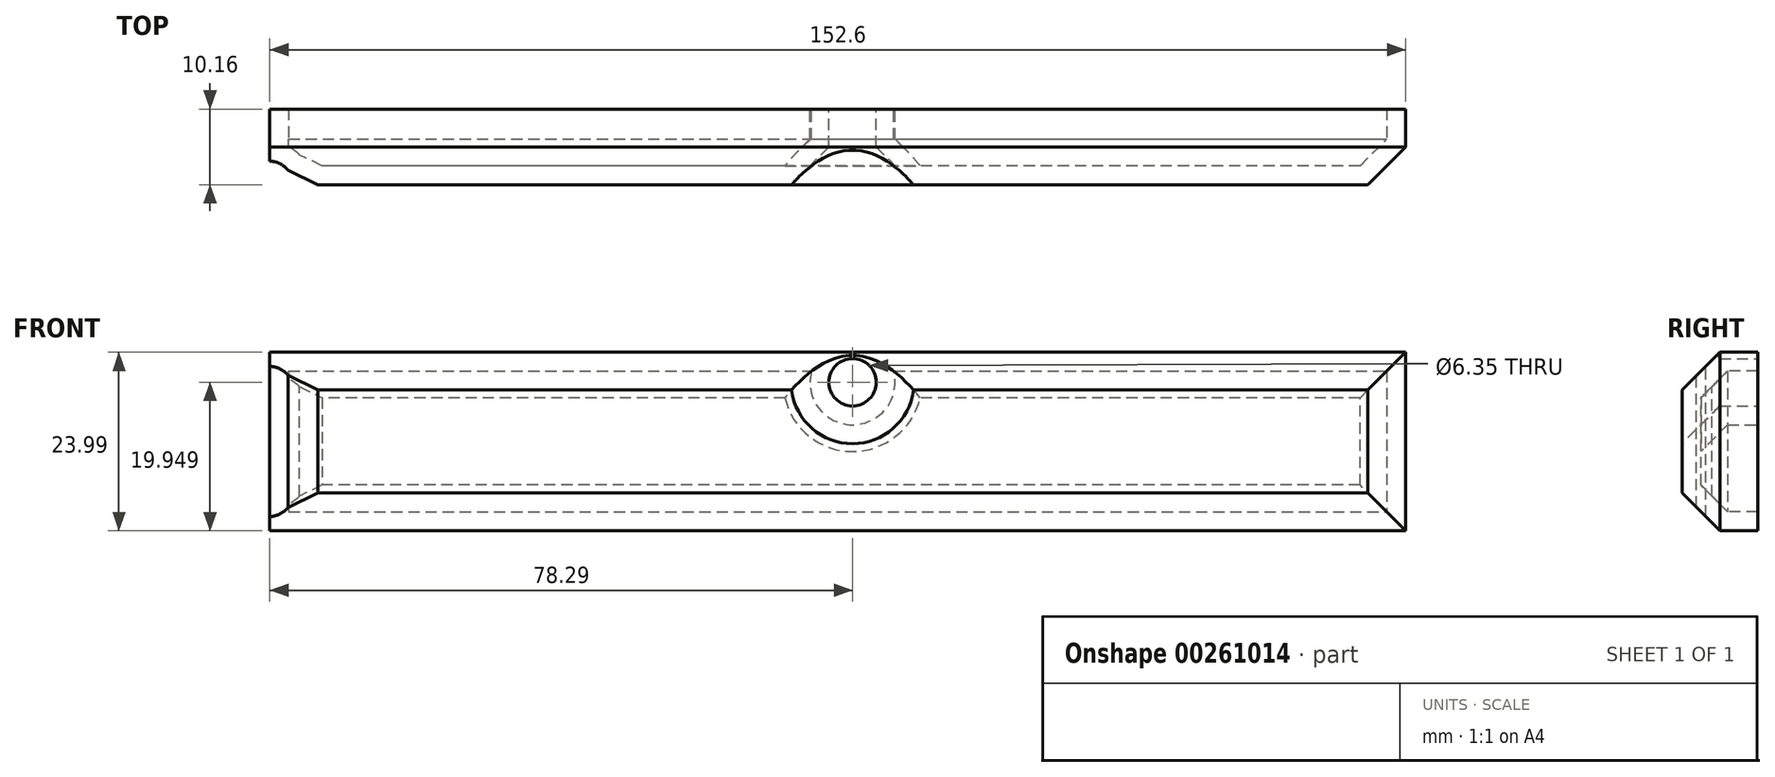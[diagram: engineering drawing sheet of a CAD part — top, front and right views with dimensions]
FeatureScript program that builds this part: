
annotation { "Feature Type Name" : "Feature", "Feature Type Description" : "" }
export const myFeature = defineFeature(function(context is Context, id is Id, definition is map)
    precondition{}
    {
        {
            var Q0;
            Q0=qCreatedBy(makeId("Front.planeOp"),FACE);
            var sketch = newSketch(context, id + "F0", { "sketchPlane" : qUnion([Q0])});
            skLineSegment(sketch, "E0", {"start": v(0, 0) * mm, "end": v(-76.65, 0) * mm});
            skLineSegment(sketch, "E1", {"start": v(0, 0) * mm, "end": v(75.95, 0) * mm});
            skLineSegment(sketch, "E2", {"start": v(-76.65, 0) * mm, "end": v(-76.65, -23.99) * mm});
            skLineSegment(sketch, "E3", {"start": v(75.95, 0) * mm, "end": v(75.95, -23.99) * mm});
            skLineSegment(sketch, "E4", {"start": v(-76.65, -23.99) * mm, "end": v(75.95, -23.99) * mm});
            skSolve(sketch);
        }
        {
            var Q0;
            Q0=qCreatedBy(makeId("Top.planeOp"),FACE);
            var sketch = newSketch(context, id + "F1", { "sketchPlane" : qUnion([Q0])});
            skLineSegment(sketch, "E5", {"start": v(-76.7, 0) * mm, "end": v(-76.7, 10.03) * mm});
            skLineSegment(sketch, "E6", {"start": v(75.65, 0) * mm, "end": v(75.65, 10.03) * mm});
            skLineSegment(sketch, "E7", {"start": v(-76.7, 10.03) * mm, "end": v(75.65, 10.03) * mm});
            skSolve(sketch);
        }
        {
            var Q0;
            Q0=makeQuery(id+"F0.imprint","IMPRINT",FACE,{"disambiguationData":[TD([[makeQuery(id+"F0.imprint","IMPRINT",EDGE,{"derivedFrom":sQuery(id+"F0.wireOp",EDGE,"E0")}),1.0]])]});
            extrude(context, id + "F2", {"entities" : qUnion([Q0]), "oppositeDirection" : true, "depth" : 10.16 * mm});
        }
        {
            var Q0;
            Q0=sQuery(id+"F1.wireOp",VERTEX,"E5.start");
            var Q1;
            Q1=makeQuery(id+"F2.opExtrude","SWEPT_BODY",BODY,{"disambiguationData":[OSD([sQuery(id+"F0.wireOp",EDGE,"E0"),sQuery(id+"F0.wireOp",EDGE,"E1"),sQuery(id+"F0.wireOp",EDGE,"E2"),sQuery(id+"F0.wireOp",EDGE,"E3"),sQuery(id+"F0.wireOp",EDGE,"E4")])]});
            hole(context, id + "F3", {"style" : HoleStyle.SIMPLE, "endStyle" : HoleEndStyle.THROUGH, "holeDiameter" : 6.35 * mm, "tappedDepth" : 12.7 * mm, "tapClearance" : 3, "locations" : qUnion([Q0]), "scope" : qUnion([Q1])});
        }
        {
            var Q0;
            Q0=makeQuery(id+"F2.opExtrude","CAP_FACE",FACE,{"disambiguationData":[OSD([sQuery(id+"F0.wireOp",EDGE,"E0"),sQuery(id+"F0.wireOp",EDGE,"E1"),sQuery(id+"F0.wireOp",EDGE,"E2"),sQuery(id+"F0.wireOp",EDGE,"E3"),sQuery(id+"F0.wireOp",EDGE,"E4")])],"isStart":false});
            var sketch = newSketch(context, id + "F4", { "sketchPlane" : qUnion([Q0])});
            skCircle(sketch, "E8", {"center": v(-1.64, -4.04) * mm, "radius": 5.96 * mm});
            skSolve(sketch);
        }
        {
            var Q0;
            Q0=sQuery(id+"F4.wireOp",VERTEX,"E8.center");
            var Q1;
            Q1=makeQuery(id+"F2.opExtrude","SWEPT_BODY",BODY,{"disambiguationData":[OSD([sQuery(id+"F0.wireOp",EDGE,"E0"),sQuery(id+"F0.wireOp",EDGE,"E1"),sQuery(id+"F0.wireOp",EDGE,"E2"),sQuery(id+"F0.wireOp",EDGE,"E3"),sQuery(id+"F0.wireOp",EDGE,"E4")])]});
            hole(context, id + "F5", {"style" : HoleStyle.SIMPLE, "endStyle" : HoleEndStyle.THROUGH, "holeDiameter" : 6.35 * mm, "tappedDepth" : 12.7 * mm, "tapClearance" : 3, "locations" : qUnion([Q0]), "scope" : qUnion([Q1])});
        }
        {
            var Q0;
            Q0=makeQuery(id+"F2.opExtrude","CAP_EDGE",EDGE,{"disambiguationData":[OSD([sQuery(id+"F0.wireOp",EDGE,"E4")])],"isStart":true});
            var Q1;
            Q1=makeQuery(id+"F2.opExtrude","CAP_FACE",FACE,{"disambiguationData":[OSD([sQuery(id+"F0.wireOp",EDGE,"E0"),sQuery(id+"F0.wireOp",EDGE,"E1"),sQuery(id+"F0.wireOp",EDGE,"E2"),sQuery(id+"F0.wireOp",EDGE,"E3"),sQuery(id+"F0.wireOp",EDGE,"E4")])],"isStart":true});
            chamfer(context, id + "F6", {"entities" : qUnion([Q0, Q1]), "width" : 5.08 * mm, "tangentPropagation" : true});
        }
        {
            var Q0;
            Q0=makeQuery(id+"F2.opExtrude","CAP_FACE",FACE,{"disambiguationData":[OSD([sQuery(id+"F0.wireOp",EDGE,"E0"),sQuery(id+"F0.wireOp",EDGE,"E1"),sQuery(id+"F0.wireOp",EDGE,"E2"),sQuery(id+"F0.wireOp",EDGE,"E3"),sQuery(id+"F0.wireOp",EDGE,"E4")])],"isStart":false});
            shell(context, id + "F7", {"entities" : qUnion([Q0]), "thickness" : 2.54 * mm});
        }
    });
